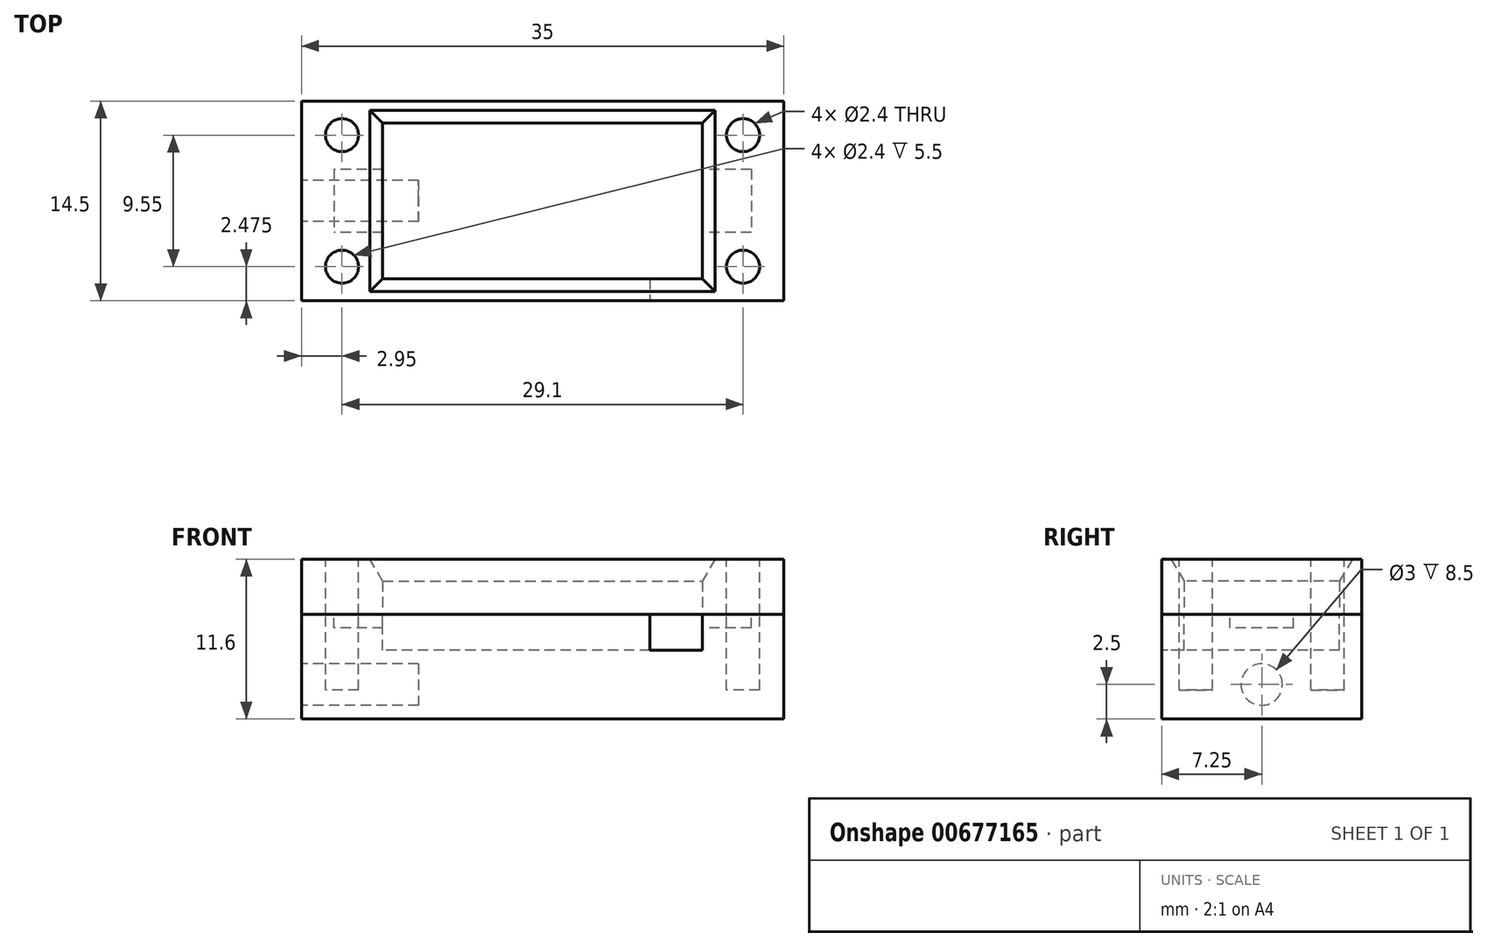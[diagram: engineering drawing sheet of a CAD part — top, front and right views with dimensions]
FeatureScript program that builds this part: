
annotation { "Feature Type Name" : "Feature", "Feature Type Description" : "" }
export const myFeature = defineFeature(function(context is Context, id is Id, definition is map)
    precondition{}
    {
        {
            var Q0;
            Q0=qCreatedBy(makeId("Top.planeOp"),FACE);
            var sketch = newSketch(context, id + "F0", { "sketchPlane" : qUnion([Q0])});
            skLineSegment(sketch, "E0.bottom", {"start": v(17.5, 7.25) * mm, "end": v(-17.5, 7.25) * mm});
            skLineSegment(sketch, "E0.top", {"start": v(17.5, -7.25) * mm, "end": v(11.6, -7.25) * mm});
            skLineSegment(sketch, "E0.left", {"start": v(17.5, 7.25) * mm, "end": v(17.5, -7.25) * mm});
            skLineSegment(sketch, "E0.right", {"start": v(-17.5, 7.25) * mm, "end": v(-17.5, -7.25) * mm});
            skPoint(sketch, "E0.middle", {"position": v(0, 0) * mm});
            skLineSegment(sketch, "E1.bottom", {"start": v(11.6, 5.65) * mm, "end": v(-11.6, 5.65) * mm});
            skLineSegment(sketch, "E1.top", {"start": v(7.8, -5.65) * mm, "end": v(-11.6, -5.65) * mm});
            skLineSegment(sketch, "E1.left", {"start": v(11.6, 5.65) * mm, "end": v(11.6, 2.3) * mm});
            skLineSegment(sketch, "E1.right", {"start": v(-11.6, 5.65) * mm, "end": v(-11.6, 2.3) * mm});
            skLineSegment(sketch, "E2.bottom", {"start": v(15.15, 2.3) * mm, "end": v(11.6, 2.3) * mm});
            skLineSegment(sketch, "E2.top", {"start": v(15.15, -2.3) * mm, "end": v(11.6, -2.3) * mm});
            skLineSegment(sketch, "E2.left", {"start": v(15.15, 2.3) * mm, "end": v(15.15, -2.3) * mm});
            skLineSegment(sketch, "E2.right", {"start": v(-15.15, 2.3) * mm, "end": v(-15.15, -2.3) * mm});
            skLineSegment(sketch, "E3.trimOffspring", {"start": v(-11.6, -2.3) * mm, "end": v(-11.6, -5.65) * mm});
            skLineSegment(sketch, "E4.trimOffspring", {"start": v(-11.6, 2.3) * mm, "end": v(-15.15, 2.3) * mm});
            skLineSegment(sketch, "E5.trimOffspring", {"start": v(-11.6, -2.3) * mm, "end": v(-15.15, -2.3) * mm});
            skLineSegment(sketch, "E6.trimOffspring", {"start": v(11.6, -2.3) * mm, "end": v(11.6, -7.25) * mm});
            skLineSegment(sketch, "E7.0", {"start": v(7.8, -5.65) * mm, "end": v(7.8, -7.25) * mm});
            skPoint(sketch, "E8.orphan", {"position": v(11.6, -5.65) * mm});
            skLineSegment(sketch, "E9.trimOffspring", {"start": v(7.8, -7.25) * mm, "end": v(-17.5, -7.25) * mm});
            skSolve(sketch);
        }
        {
            var Q0;
            Q0 = qSketchRegion(id + "F0", true);
            extrude(context, id + "F1", {"entities" : qUnion([Q0]), "oppositeDirection" : true, "depth" : 2.6 * mm, "offsetDistance" : 25 * mm});
        }
        {
            var Q0;
            Q0=makeQuery(id+"F1.opExtrude","CAP_FACE",FACE,{"disambiguationData":[OSD([sQuery(id+"F0.wireOp",EDGE,"E0.bottom"),sQuery(id+"F0.wireOp",EDGE,"E0.top"),sQuery(id+"F0.wireOp",EDGE,"E0.left"),sQuery(id+"F0.wireOp",EDGE,"E0.right"),sQuery(id+"F0.wireOp",EDGE,"E1.bottom"),sQuery(id+"F0.wireOp",EDGE,"E1.top"),sQuery(id+"F0.wireOp",EDGE,"E1.left"),sQuery(id+"F0.wireOp",EDGE,"E1.right"),sQuery(id+"F0.wireOp",EDGE,"E2.bottom"),sQuery(id+"F0.wireOp",EDGE,"E2.top"),sQuery(id+"F0.wireOp",EDGE,"E2.left"),sQuery(id+"F0.wireOp",EDGE,"E2.right"),sQuery(id+"F0.wireOp",EDGE,"E3.trimOffspring"),sQuery(id+"F0.wireOp",EDGE,"E4.trimOffspring"),sQuery(id+"F0.wireOp",EDGE,"E5.trimOffspring"),sQuery(id+"F0.wireOp",EDGE,"E6.trimOffspring"),sQuery(id+"F0.wireOp",EDGE,"E7.0"),sQuery(id+"F0.wireOp",EDGE,"E9.trimOffspring")])],"isStart":false});
            var sketch = newSketch(context, id + "F2", { "sketchPlane" : qUnion([Q0])});
            skLineSegment(sketch, "E10.0", {"start": v(-11.6, 2.3) * mm, "end": v(-15.15, 2.3) * mm});
            skLineSegment(sketch, "E11.0", {"start": v(-15.15, -2.3) * mm, "end": v(-15.15, 2.3) * mm});
            skLineSegment(sketch, "E12.0", {"start": v(-11.6, -2.3) * mm, "end": v(-15.15, -2.3) * mm});
            skLineSegment(sketch, "E13.0", {"start": v(15.15, -2.3) * mm, "end": v(11.6, -2.3) * mm});
            skLineSegment(sketch, "E14.0", {"start": v(15.15, -2.3) * mm, "end": v(15.15, 2.3) * mm});
            skLineSegment(sketch, "E15.0", {"start": v(15.15, 2.3) * mm, "end": v(11.6, 2.3) * mm});
            skLineSegment(sketch, "E16", {"start": v(-11.6, 2.3) * mm, "end": v(-11.6, -2.3) * mm});
            skLineSegment(sketch, "E17", {"start": v(11.6, 2.3) * mm, "end": v(11.6, -2.3) * mm});
            skSolve(sketch);
        }
        {
            var Q0;
            Q0 = qSketchRegion(id + "F2", true);
            var Q1;
            Q1=makeQuery(id+"F1.opExtrude","CAP_FACE",FACE,{"disambiguationData":[OSD([sQuery(id+"F0.wireOp",EDGE,"E0.bottom"),sQuery(id+"F0.wireOp",EDGE,"E0.top"),sQuery(id+"F0.wireOp",EDGE,"E0.left"),sQuery(id+"F0.wireOp",EDGE,"E0.right"),sQuery(id+"F0.wireOp",EDGE,"E1.bottom"),sQuery(id+"F0.wireOp",EDGE,"E1.top"),sQuery(id+"F0.wireOp",EDGE,"E1.left"),sQuery(id+"F0.wireOp",EDGE,"E1.right"),sQuery(id+"F0.wireOp",EDGE,"E2.bottom"),sQuery(id+"F0.wireOp",EDGE,"E2.top"),sQuery(id+"F0.wireOp",EDGE,"E2.left"),sQuery(id+"F0.wireOp",EDGE,"E2.right"),sQuery(id+"F0.wireOp",EDGE,"E3.trimOffspring"),sQuery(id+"F0.wireOp",EDGE,"E4.trimOffspring"),sQuery(id+"F0.wireOp",EDGE,"E5.trimOffspring"),sQuery(id+"F0.wireOp",EDGE,"E6.trimOffspring"),sQuery(id+"F0.wireOp",EDGE,"E7.0"),sQuery(id+"F0.wireOp",EDGE,"E9.trimOffspring")])],"isStart":true});
            extrude(context, id + "F3", {"entities" : qUnion([Q0]), "operationType" : NewBodyOperationType.ADD, "endBound" : BoundingType.UP_TO_SURFACE, "oppositeDirection" : true, "depth" : 25 * mm, "endBoundEntityFace" : qUnion([Q1]), "hasOffset" : true, "offsetDistance" : 1 * mm});
        }
        {
            var Q0;
            Q0=makeQuery(id+"F3.boolean.opBoolean","MERGE",FACE,{"derivedFrom":[makeQuery(id+"F1.opExtrude","CAP_FACE",FACE,{"disambiguationData":[OSD([sQuery(id+"F0.wireOp",EDGE,"E0.bottom"),sQuery(id+"F0.wireOp",EDGE,"E0.top"),sQuery(id+"F0.wireOp",EDGE,"E0.left"),sQuery(id+"F0.wireOp",EDGE,"E0.right"),sQuery(id+"F0.wireOp",EDGE,"E1.bottom"),sQuery(id+"F0.wireOp",EDGE,"E1.top"),sQuery(id+"F0.wireOp",EDGE,"E1.left"),sQuery(id+"F0.wireOp",EDGE,"E1.right"),sQuery(id+"F0.wireOp",EDGE,"E2.bottom"),sQuery(id+"F0.wireOp",EDGE,"E2.top"),sQuery(id+"F0.wireOp",EDGE,"E2.left"),sQuery(id+"F0.wireOp",EDGE,"E2.right"),sQuery(id+"F0.wireOp",EDGE,"E3.trimOffspring"),sQuery(id+"F0.wireOp",EDGE,"E4.trimOffspring"),sQuery(id+"F0.wireOp",EDGE,"E5.trimOffspring"),sQuery(id+"F0.wireOp",EDGE,"E6.trimOffspring"),sQuery(id+"F0.wireOp",EDGE,"E7.0"),sQuery(id+"F0.wireOp",EDGE,"E9.trimOffspring")])],"isStart":false}),makeQuery(id+"F3.opExtrude","CAP_FACE",FACE,{"disambiguationData":[OSD([sQuery(id+"F2.wireOp",EDGE,"E10.0"),sQuery(id+"F2.wireOp",EDGE,"E11.0"),sQuery(id+"F2.wireOp",EDGE,"E12.0"),sQuery(id+"F2.wireOp",EDGE,"E16")])],"isStart":true}),makeQuery(id+"F3.opExtrude","CAP_FACE",FACE,{"disambiguationData":[OSD([sQuery(id+"F2.wireOp",EDGE,"E13.0"),sQuery(id+"F2.wireOp",EDGE,"E14.0"),sQuery(id+"F2.wireOp",EDGE,"E15.0"),sQuery(id+"F2.wireOp",EDGE,"E17")])],"isStart":true})]});
            var sketch = newSketch(context, id + "F4", { "sketchPlane" : qUnion([Q0])});
            skLineSegment(sketch, "E18.bottom", {"start": v(-17.5, 7.25) * mm, "end": v(17.5, 7.25) * mm});
            skLineSegment(sketch, "E18.top", {"start": v(-17.5, -7.25) * mm, "end": v(17.5, -7.25) * mm});
            skLineSegment(sketch, "E18.left", {"start": v(-17.5, 7.25) * mm, "end": v(-17.5, -7.25) * mm});
            skLineSegment(sketch, "E18.right", {"start": v(17.5, 7.25) * mm, "end": v(17.5, -7.25) * mm});
            skSolve(sketch);
        }
        {
            var Q0;
            Q0 = qSketchRegion(id + "F4", true);
            extrude(context, id + "F5", {"entities" : qUnion([Q0]), "operationType" : NewBodyOperationType.ADD, "depth" : 5 * mm, "offsetDistance" : 25 * mm});
        }
        {
            var Q0;
            Q0=makeQuery(id+"F5.boolean.opBoolean","MERGE",FACE,{"derivedFrom":[makeQuery(id+"F1.opExtrude","SWEPT_FACE",FACE,{"disambiguationData":[OSD([sQuery(id+"F0.wireOp",EDGE,"E0.right")])]}),makeQuery(id+"F5.opExtrude","SWEPT_FACE",FACE,{"disambiguationData":[OSD([sQuery(id+"F4.wireOp",EDGE,"E18.left")])]})]});
            var sketch = newSketch(context, id + "F6", { "sketchPlane" : qUnion([Q0])});
            skCircle(sketch, "E19", {"center": v(0, -5.1) * mm, "radius": 1.5 * mm});
            skPoint(sketch, "E19.centerSnap0", {"position": v(0, -7.6) * mm});
            skSolve(sketch);
        }
        {
            var Q0;
            Q0 = qSketchRegion(id + "F6", true);
            extrude(context, id + "F7", {"entities" : qUnion([Q0]), "operationType" : NewBodyOperationType.REMOVE, "oppositeDirection" : true, "depth" : 8.5 * mm, "offsetDistance" : 25 * mm});
        }
        {
            var Q0;
            Q0=makeQuery(id+"F1.opExtrude","CAP_FACE",FACE,{"disambiguationData":[OSD([sQuery(id+"F0.wireOp",EDGE,"E0.bottom"),sQuery(id+"F0.wireOp",EDGE,"E0.top"),sQuery(id+"F0.wireOp",EDGE,"E0.left"),sQuery(id+"F0.wireOp",EDGE,"E0.right"),sQuery(id+"F0.wireOp",EDGE,"E1.bottom"),sQuery(id+"F0.wireOp",EDGE,"E1.top"),sQuery(id+"F0.wireOp",EDGE,"E1.left"),sQuery(id+"F0.wireOp",EDGE,"E1.right"),sQuery(id+"F0.wireOp",EDGE,"E2.bottom"),sQuery(id+"F0.wireOp",EDGE,"E2.top"),sQuery(id+"F0.wireOp",EDGE,"E2.left"),sQuery(id+"F0.wireOp",EDGE,"E2.right"),sQuery(id+"F0.wireOp",EDGE,"E3.trimOffspring"),sQuery(id+"F0.wireOp",EDGE,"E4.trimOffspring"),sQuery(id+"F0.wireOp",EDGE,"E5.trimOffspring"),sQuery(id+"F0.wireOp",EDGE,"E6.trimOffspring"),sQuery(id+"F0.wireOp",EDGE,"E7.0"),sQuery(id+"F0.wireOp",EDGE,"E9.trimOffspring")])],"isStart":true});
            var sketch = newSketch(context, id + "F8", { "sketchPlane" : qUnion([Q0])});
            skLineSegment(sketch, "E20.bottom", {"start": v(-17.5, 7.25) * mm, "end": v(17.5, 7.25) * mm});
            skLineSegment(sketch, "E20.top", {"start": v(-17.5, -7.25) * mm, "end": v(17.5, -7.25) * mm});
            skLineSegment(sketch, "E20.left", {"start": v(-17.5, 7.25) * mm, "end": v(-17.5, -7.25) * mm});
            skLineSegment(sketch, "E20.right", {"start": v(17.5, 7.25) * mm, "end": v(17.5, -7.25) * mm});
            skLineSegment(sketch, "E21.bottom", {"start": v(-11.6, 5.65) * mm, "end": v(11.6, 5.65) * mm});
            skLineSegment(sketch, "E21.top", {"start": v(-11.6, -5.65) * mm, "end": v(11.6, -5.65) * mm});
            skLineSegment(sketch, "E21.left", {"start": v(-11.6, 5.65) * mm, "end": v(-11.6, -5.65) * mm});
            skLineSegment(sketch, "E21.right", {"start": v(11.6, 5.65) * mm, "end": v(11.6, -5.65) * mm});
            skSolve(sketch);
        }
        {
            var Q0;
            Q0 = qSketchRegion(id + "F8", true);
            extrude(context, id + "F9", {"entities" : qUnion([Q0]), "depth" : 4 * mm, "offsetDistance" : 25 * mm});
        }
        {
            var Q0;
            Q0=makeQuery(id+"F1.opExtrude","CAP_FACE",FACE,{"disambiguationData":[OSD([sQuery(id+"F0.wireOp",EDGE,"E0.bottom"),sQuery(id+"F0.wireOp",EDGE,"E0.top"),sQuery(id+"F0.wireOp",EDGE,"E0.left"),sQuery(id+"F0.wireOp",EDGE,"E0.right"),sQuery(id+"F0.wireOp",EDGE,"E1.bottom"),sQuery(id+"F0.wireOp",EDGE,"E1.top"),sQuery(id+"F0.wireOp",EDGE,"E1.left"),sQuery(id+"F0.wireOp",EDGE,"E1.right"),sQuery(id+"F0.wireOp",EDGE,"E2.bottom"),sQuery(id+"F0.wireOp",EDGE,"E2.top"),sQuery(id+"F0.wireOp",EDGE,"E2.left"),sQuery(id+"F0.wireOp",EDGE,"E2.right"),sQuery(id+"F0.wireOp",EDGE,"E3.trimOffspring"),sQuery(id+"F0.wireOp",EDGE,"E4.trimOffspring"),sQuery(id+"F0.wireOp",EDGE,"E5.trimOffspring"),sQuery(id+"F0.wireOp",EDGE,"E6.trimOffspring"),sQuery(id+"F0.wireOp",EDGE,"E7.0"),sQuery(id+"F0.wireOp",EDGE,"E9.trimOffspring")])],"isStart":true});
            var sketch = newSketch(context, id + "F10", { "sketchPlane" : qUnion([Q0])});
            skLineSegment(sketch, "E22", {"start": v(-14.55, 7.25) * mm, "end": v(-14.55, 2.3) * mm, "construction": true});
            skLineSegment(sketch, "E23", {"start": v(-17.5, 4.77) * mm, "end": v(-11.6, 4.77) * mm, "construction": true});
            skPoint(sketch, "E23.startSnap0", {"position": v(-14.55, 4.77) * mm});
            skCircle(sketch, "E24", {"center": v(-14.55, 4.77) * mm, "radius": 1.2 * mm});
            skCircle(sketch, "E25.MirrorC", {"center": v(14.55, 4.77) * mm, "radius": 1.2 * mm});
            skCircle(sketch, "E26.MirrorC", {"center": v(-14.55, -4.77) * mm, "radius": 1.2 * mm});
            skCircle(sketch, "E27.MirrorC", {"center": v(14.55, -4.77) * mm, "radius": 1.2 * mm});
            skSolve(sketch);
        }
        {
            var Q0;
            Q0 = qSketchRegion(id + "F10", true);
            extrude(context, id + "F11", {"entities" : qUnion([Q0]), "operationType" : NewBodyOperationType.REMOVE, "oppositeDirection" : true, "depth" : 5.5 * mm, "offsetDistance" : 25 * mm, "hasSecondDirection" : true, "secondDirectionBound" : SecondDirectionBoundingType.THROUGH_ALL, "secondDirectionOppositeDirection" : false, "secondDirectionDepth" : 25 * mm});
        }
        {
            var Q0;
            Q0=makeQuery(id+"F9.opExtrude","CAP_EDGE",EDGE,{"disambiguationData":[OSD([sQuery(id+"F8.wireOp",EDGE,"E21.left")])],"isStart":false});
            var Q1;
            Q1=makeQuery(id+"F9.opExtrude","CAP_EDGE",EDGE,{"disambiguationData":[OSD([sQuery(id+"F8.wireOp",EDGE,"E21.bottom")])],"isStart":false});
            var Q2;
            Q2=makeQuery(id+"F9.opExtrude","CAP_EDGE",EDGE,{"disambiguationData":[OSD([sQuery(id+"F8.wireOp",EDGE,"E21.right")])],"isStart":false});
            var Q3;
            Q3=makeQuery(id+"F9.opExtrude","CAP_EDGE",EDGE,{"disambiguationData":[OSD([sQuery(id+"F8.wireOp",EDGE,"E21.top")])],"isStart":false});
            chamfer(context, id + "F12", {"entities" : qUnion([Q0, Q1, Q2, Q3]), "chamferType" : ChamferType.OFFSET_ANGLE, "width" : 1.6 * mm, "oppositeDirection" : false, "angle" : 30 * degree, "tangentPropagation" : true});
        }
    });
